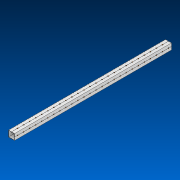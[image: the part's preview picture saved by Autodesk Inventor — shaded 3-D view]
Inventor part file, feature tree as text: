
AUTODESK INVENTOR PART (.ipt)
format: ipt  version: 2022.2 (Build 262287000, 287)  size: 851,456 bytes
history: native  units: in
note: dims shown in document units (in); Inventor stores cm internally (conversion verified against a paired STEP export)
features: other x52, pattern_linear x2, extrude x1, sketch x1
ambient origin geometry x8: Origin, YZ Plane, XZ Plane, XY Plane, X Axis, Y Axis, Z Axis, Center Point
bodies: Solid1 (feature_tree)
feature tree (56):
  extrude  "Extrusion1"  TaperAngle=0.0deg  [1 undecoded]
  other  "Work Axis1"
  other  "Work Axis2"
  pattern_linear  "Rectangular Pattern1"  Count1=26  [1 undecoded]
  pattern_linear  "Rectangular Pattern2"  Spacing1=1.0in  [1 undecoded]
  sketch  "Sketch1"  dims[d0=33.0in d1=0.0in d2=10.2362in d4=1.0in d5=9.8425in d7=1.0in]
  other  "Work Axis3"
  other  "Work Axis4"
  other  "Work Axis5"
  other  "Work Axis6"
  other  "Work Axis7"
  other  "Work Axis8"
  other  "Work Axis9"
  other  "Work Axis10"
  other  "Work Axis11"
  other  "Work Axis12"
  other  "Work Axis13"
  other  "Work Axis14"
  other  "Work Axis15"
  other  "Work Axis16"
  other  "Work Axis17"
  other  "Work Axis18"
  other  "Work Axis19"
  other  "Work Axis20"
  other  "Work Axis21"
  other  "Work Axis22"
  other  "Work Axis23"
  other  "Work Axis24"
  other  "Work Axis25"
  other  "Work Axis26"
  other  "Work Axis27"
  other  "Work Axis28"
  other  "Work Axis29"
  other  "Work Axis63"
  other  "Work Axis64"
  other  "Work Axis65"
  other  "Work Axis66"
  other  "Work Axis67"
  other  "Work Axis68"
  other  "Work Axis69"
  other  "Work Axis70"
  other  "Work Axis71"
  other  "Work Axis72"
  other  "Work Axis73"
  other  "Work Axis74"
  other  "Work Axis75"
  other  "Work Axis76"
  other  "Work Axis77"
  other  "Work Axis78"
  other  "Work Axis79"
  other  "Work Axis80"
  other  "Work Axis81"
  other  "Work Axis82"
  other  "Work Axis83"
  other  "Work Axis84"
  other  "LPattern2"
note: 3 required parameter values undecoded (feature->parameter linkage not recoverable at this tier; creation-order binding heuristic only, values carry confidence <= 0.55)
